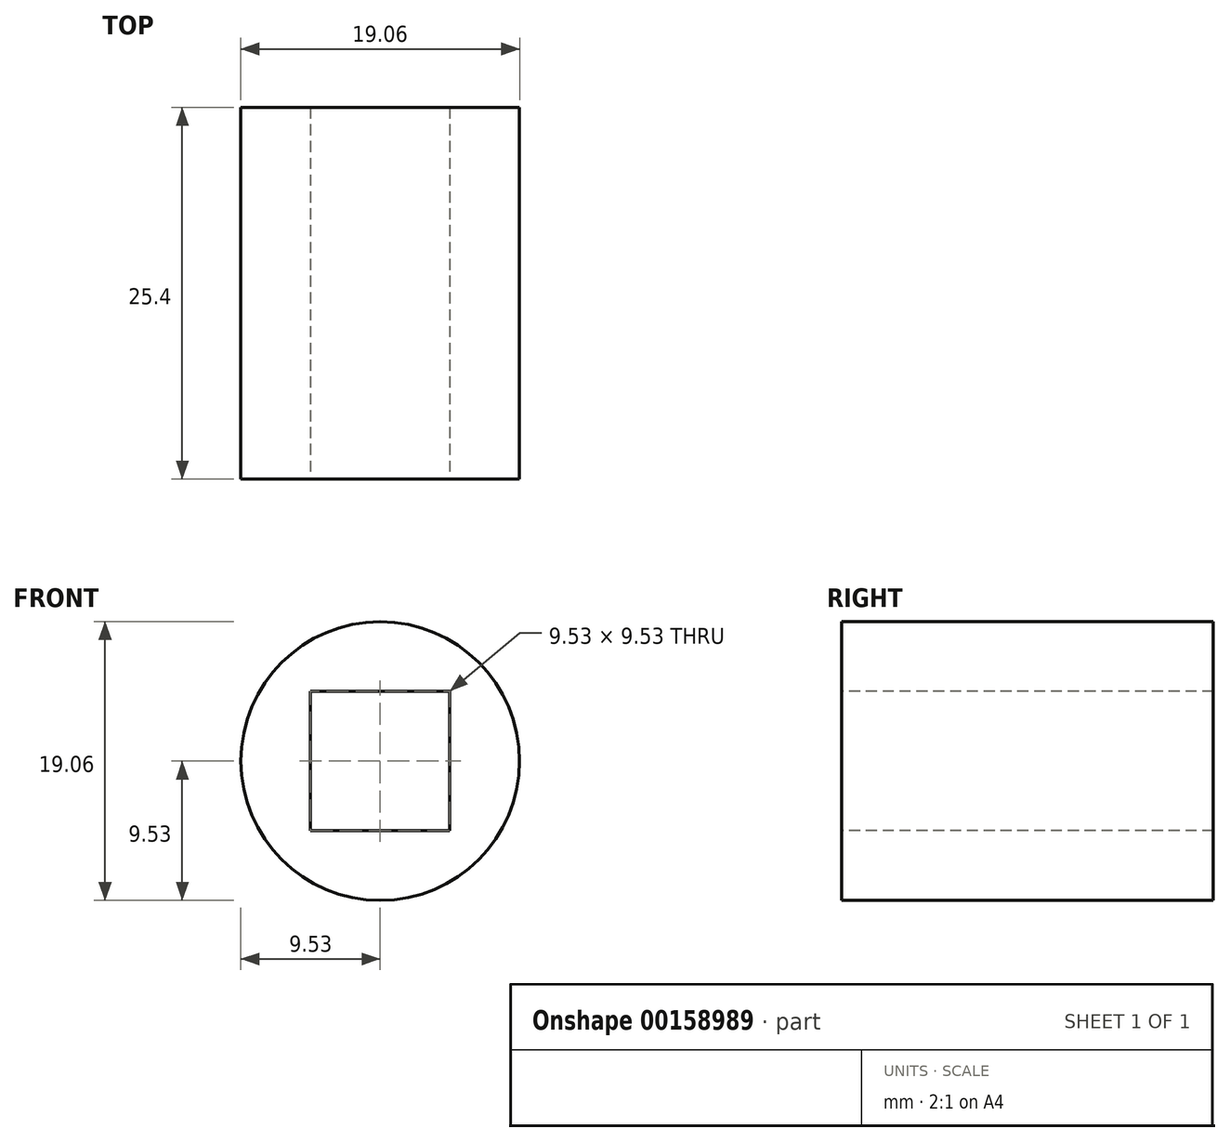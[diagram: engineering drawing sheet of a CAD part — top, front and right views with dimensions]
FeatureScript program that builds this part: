
annotation { "Feature Type Name" : "Feature", "Feature Type Description" : "" }
export const myFeature = defineFeature(function(context is Context, id is Id, definition is map)
    precondition{}
    {
        {
            var Q0;
            Q0=qCreatedBy(makeId("Front.planeOp"),FACE);
            var sketch = newSketch(context, id + "F0", { "sketchPlane" : qUnion([Q0])});
            skCircle(sketch, "E0", {"center": v(0, 0) * mm, "radius": 9.53 * mm});
            skSolve(sketch);
        }
        {
            var Q0;
            Q0 = qSketchRegion(id + "F0", true);
            extrude(context, id + "F1", {"entities" : qUnion([Q0]), "depth" : 25.4 * mm});
        }
        {
            var Q0;
            Q0=makeQuery(id+"F1.opExtrude","CAP_FACE",FACE,{"disambiguationData":[OSD([sQuery(id+"F0.wireOp",EDGE,"E0")])],"isStart":false});
            var sketch = newSketch(context, id + "F2", { "sketchPlane" : qUnion([Q0])});
            skLineSegment(sketch, "E1.bottom", {"start": v(4.76, 4.76) * mm, "end": v(-4.76, 4.76) * mm});
            skLineSegment(sketch, "E1.top", {"start": v(4.76, -4.76) * mm, "end": v(-4.76, -4.76) * mm});
            skLineSegment(sketch, "E1.left", {"start": v(4.76, 4.76) * mm, "end": v(4.76, -4.76) * mm});
            skLineSegment(sketch, "E1.right", {"start": v(-4.76, 4.76) * mm, "end": v(-4.76, -4.76) * mm});
            skPoint(sketch, "E1.middle", {"position": v(0, 0) * mm});
            skCircle(sketch, "E2", {"center": v(0, 0) * mm, "radius": 4.76 * mm});
            skSolve(sketch);
        }
        {
            var Q0;
            {var subQ0=sQuery(id+"F2.wireOp",EDGE,"E2");var subQ1=makeQuery(id+"F2.imprint","INTERSECT",VERTEX,{"derivedFrom":[sQuery(id+"F2.wireOp",EDGE,"E1.bottom"),subQ0]});Q0=makeQuery(id+"F2.imprint","IMPRINT",FACE,{"disambiguationData":[TD([[makeQuery(id+"F2.imprint","IMPRINT",EDGE,{"disambiguationData":[TD([[subQ1,1.0]])],"derivedFrom":subQ0}),1.0]])]});}
            extrude(context, id + "F3", {"entities" : qUnion([Q0]), "operationType" : NewBodyOperationType.REMOVE, "endBound" : BoundingType.THROUGH_ALL, "oppositeDirection" : true, "depth" : 25.4 * mm});
        }
        {
            var Q0;
            Q0 = qSketchRegion(id + "F2", true);
            extrude(context, id + "F4", {"entities" : qUnion([Q0]), "operationType" : NewBodyOperationType.REMOVE, "oppositeDirection" : true, "depth" : 25.4 * mm});
        }
    });
